# Revit family: Speciality_Equipment-Cord_Reel-Hubbell_Wiring-System_HBLSS45123
name_source: partatom
category: Specialty Equipment
revit_build: Autodesk Revit 2015 (Build: 20160512_0715(x64)
units: mm (PartAtom-declared; Revit-internal decimal feet)

## types (1)
- HBLSS45123
    Amps = 20 A
    Assembly Code = D5090900
    Cover Material = Metal-Hubbell-Black
    Default Elevation = 0 "
    Description = Stainless steel reel without cord ends
    Edition number = 1
    Electrical Connector Description = Stainless Steel Cord Reel
    Hardware Material = Metal-Hubbell-Steel
    Housing Material = Metal-Hubbell-Black
    Manufacturer = Hubbell Wiring Device-Kellems
    Model = HBLSS45123
    Product Documentation Link = https://hubbellcdn.com
    Product Guid = 01dece22-5c74-4ef5-87ae-997387ae3950
    Product Page URL = https://www.hubbell.com
    Product data url = https://bimobject.com
    URL = http://www.hubbell-wiring.com
    Voltage = 125 V

## geometry (parser evidence)
native form markers: Blend x4, Sweep x2
no freeform markers — native parametric forms only
